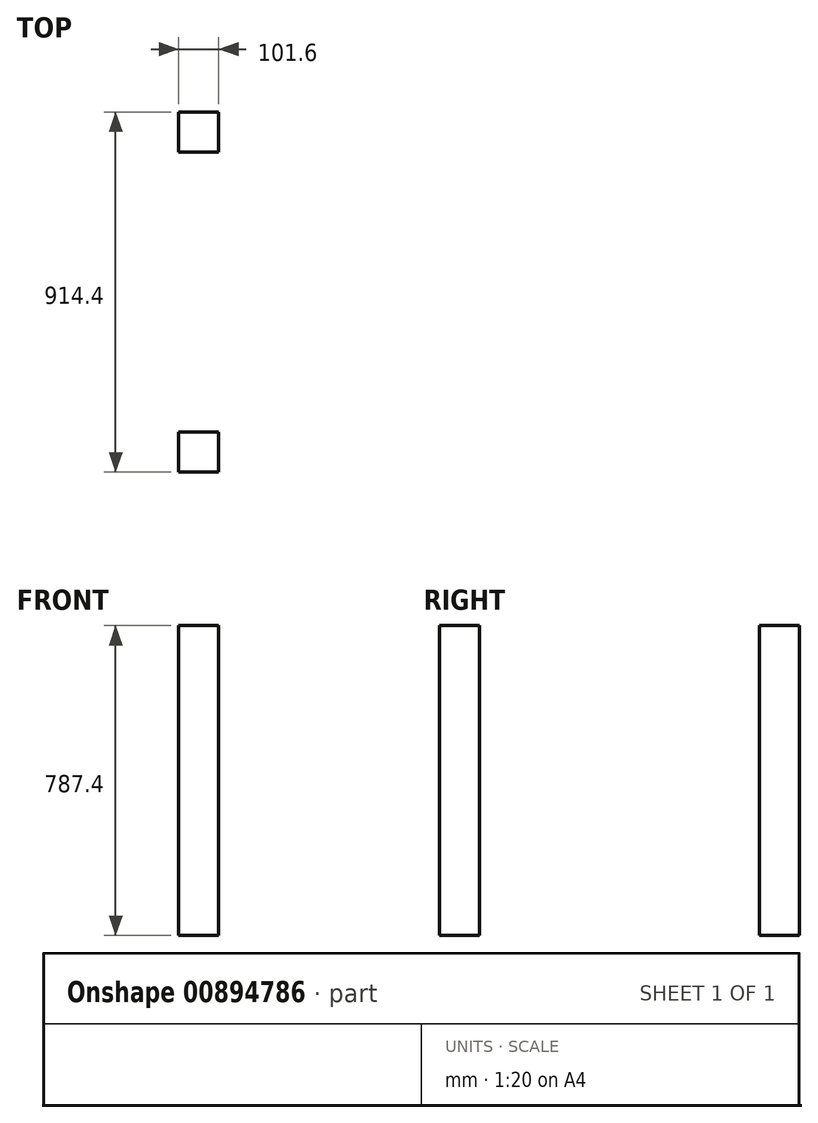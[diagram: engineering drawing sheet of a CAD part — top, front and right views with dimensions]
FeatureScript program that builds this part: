
annotation { "Feature Type Name" : "Feature", "Feature Type Description" : "" }
export const myFeature = defineFeature(function(context is Context, id is Id, definition is map)
    precondition{}
    {
        {
            var Q0;
            Q0=qCreatedBy(makeId("Top.planeOp"),FACE);
            var sketch = newSketch(context, id + "F0", { "sketchPlane" : qUnion([Q0])});
            skLineSegment(sketch, "E0.bottom", {"start": v(1206.5, 914.4) * mm, "end": v(1308.1, 914.4) * mm});
            skLineSegment(sketch, "E0.top", {"start": v(1206.5, 812.8) * mm, "end": v(1308.1, 812.8) * mm});
            skLineSegment(sketch, "E0.left", {"start": v(1206.5, 914.4) * mm, "end": v(1206.5, 812.8) * mm});
            skLineSegment(sketch, "E0.right", {"start": v(1308.1, 914.4) * mm, "end": v(1308.1, 812.8) * mm});
            skLineSegment(sketch, "E1.bottom", {"start": v(1206.5, 812.8) * mm, "end": v(1308.1, 812.8) * mm, "construction": true});
            skLineSegment(sketch, "E1.left", {"start": v(1206.5, 812.8) * mm, "end": v(1206.5, 101.6) * mm, "construction": true});
            skLineSegment(sketch, "E1.right", {"start": v(1308.1, 812.8) * mm, "end": v(1308.1, 101.6) * mm, "construction": true});
            skLineSegment(sketch, "E2.bottom", {"start": v(1206.5, 101.6) * mm, "end": v(1308.1, 101.6) * mm});
            skLineSegment(sketch, "E2.top", {"start": v(1206.5, 0) * mm, "end": v(1308.1, 0) * mm});
            skLineSegment(sketch, "E2.left", {"start": v(1206.5, 101.6) * mm, "end": v(1206.5, 0) * mm});
            skLineSegment(sketch, "E2.right", {"start": v(1308.1, 101.6) * mm, "end": v(1308.1, 0) * mm});
            skLineSegment(sketch, "E3", {"start": v(0, 0) * mm, "end": v(1206.5, 0) * mm, "construction": true});
            skSolve(sketch);
        }
        {
            var Q0;
            Q0 = qSketchRegion(id + "F0", true);
            extrude(context, id + "F1", {"entities" : qUnion([Q0]), "depth" : 787.4 * mm, "offsetDistance" : 25.4 * mm});
        }
    });
